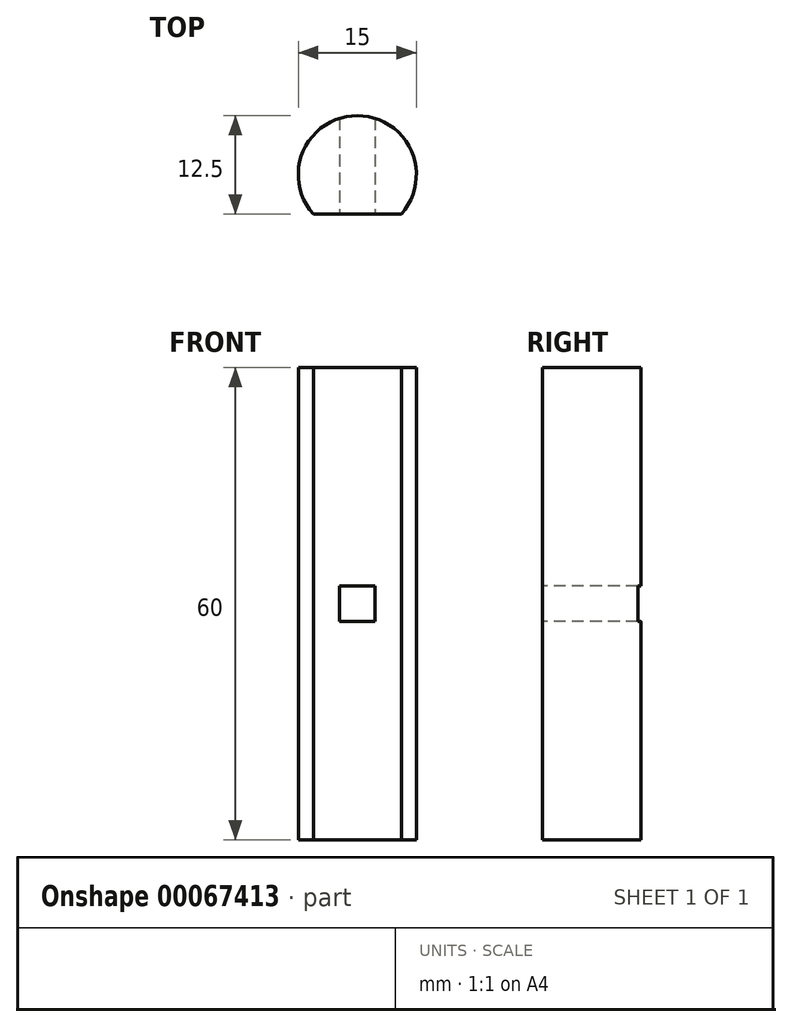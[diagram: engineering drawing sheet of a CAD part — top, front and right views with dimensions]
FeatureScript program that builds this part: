
annotation { "Feature Type Name" : "Feature", "Feature Type Description" : "" }
export const myFeature = defineFeature(function(context is Context, id is Id, definition is map)
    precondition{}
    {
        {
            var Q0;
            Q0=qCreatedBy(makeId("Top.planeOp"),FACE);
            var sketch = newSketch(context, id + "F0", { "sketchPlane" : qUnion([Q0])});
            skArc(sketch, "E0", {"start": v(5.6, -5) * mm, "mid": v(0, 7.5) * mm, "end": v(-5.6, -5) * mm});
            skLineSegment(sketch, "E1", {"start": v(-5.6, -5) * mm, "end": v(5.6, -5) * mm});
            skSolve(sketch);
        }
        {
            var Q0;
            Q0=makeQuery(id+"F0.imprint","IMPRINT",FACE,{"disambiguationData":[TD([[makeQuery(id+"F0.imprint","IMPRINT",EDGE,{"derivedFrom":sQuery(id+"F0.wireOp",EDGE,"E0")}),1.0]])]});
            extrude(context, id + "F1", {"entities" : qUnion([Q0]), "depth" : 60 * mm});
        }
        {
            var Q0;
            Q0=qCreatedBy(makeId("Front.planeOp"),FACE);
            var sketch = newSketch(context, id + "F2", { "sketchPlane" : qUnion([Q0])});
            skLineSegment(sketch, "E2.bottom", {"start": v(-2.25, 32.25) * mm, "end": v(2.25, 32.25) * mm});
            skLineSegment(sketch, "E2.top", {"start": v(-2.25, 27.75) * mm, "end": v(2.25, 27.75) * mm});
            skLineSegment(sketch, "E2.left", {"start": v(-2.25, 32.25) * mm, "end": v(-2.25, 27.75) * mm});
            skLineSegment(sketch, "E2.right", {"start": v(2.25, 32.25) * mm, "end": v(2.25, 27.75) * mm});
            skPoint(sketch, "E2.middle", {"position": v(0, 30) * mm});
            skSolve(sketch);
        }
        {
            var Q0;
            Q0 = qSketchRegion(id + "F2", true);
            extrude(context, id + "F3", {"entities" : qUnion([Q0]), "operationType" : NewBodyOperationType.REMOVE, "endBound" : BoundingType.SYMMETRIC, "oppositeDirection" : true, "depth" : 20 * mm});
        }
    });
